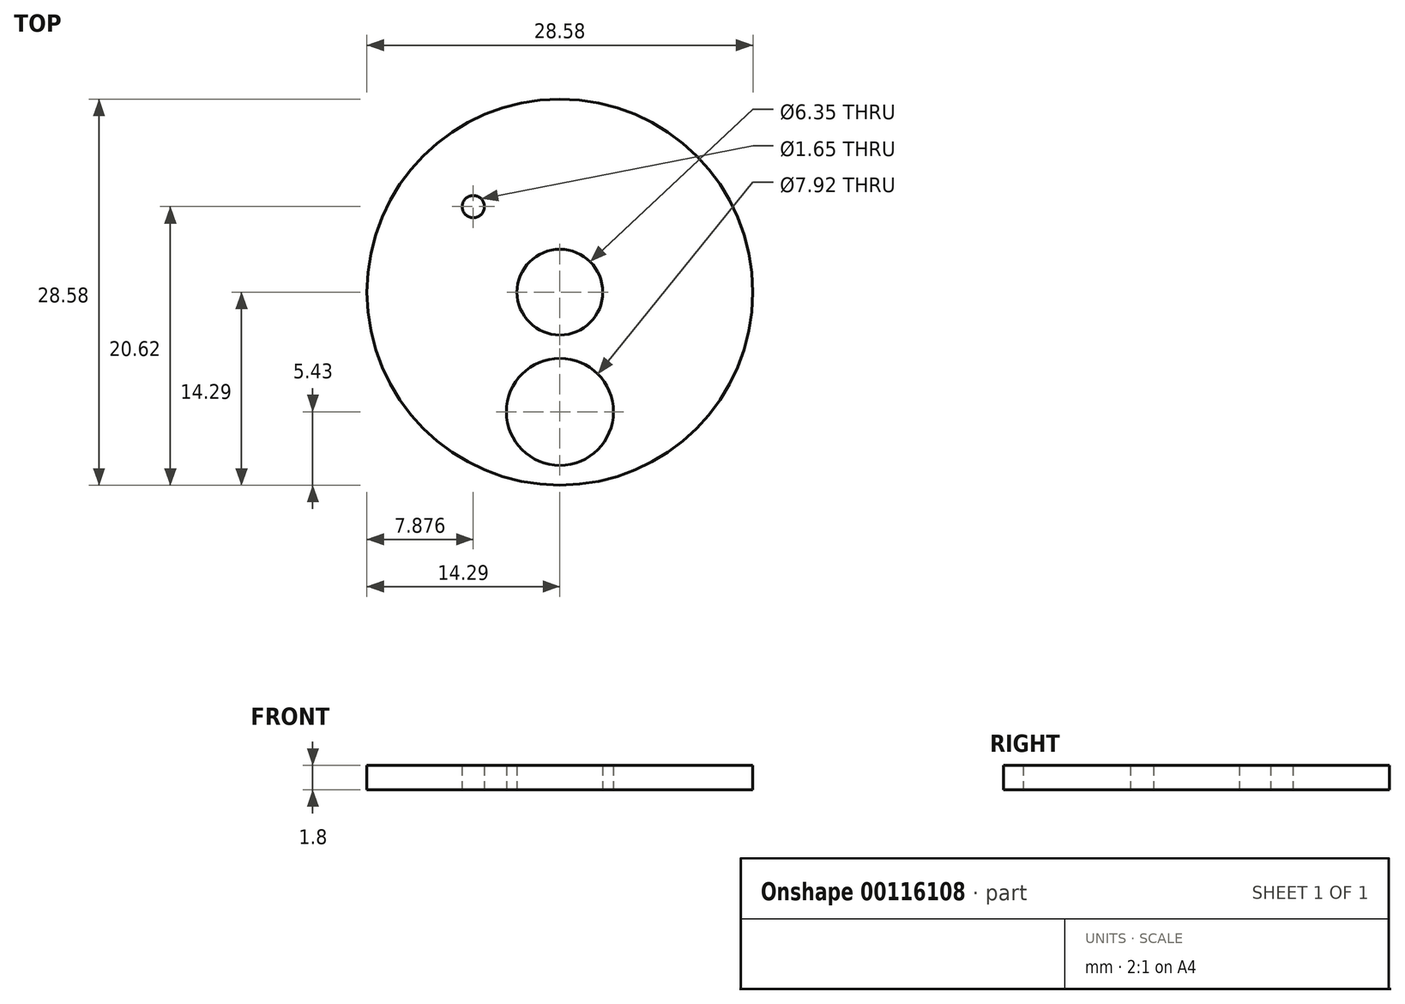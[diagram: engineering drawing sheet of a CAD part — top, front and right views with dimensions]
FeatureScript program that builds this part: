
annotation { "Feature Type Name" : "Feature", "Feature Type Description" : "" }
export const myFeature = defineFeature(function(context is Context, id is Id, definition is map)
    precondition{}
    {
        {
            var Q0;
            Q0=qCreatedBy(makeId("Top.planeOp"),FACE);
            var sketch = newSketch(context, id + "F0", { "sketchPlane" : qUnion([Q0])});
            skCircle(sketch, "E0", {"center": v(0, 0) * mm, "radius": 14.29 * mm});
            skCircle(sketch, "E1", {"center": v(0, 0) * mm, "radius": 3.18 * mm});
            skCircle(sketch, "E2", {"center": v(-6.41, 6.33) * mm, "radius": 0.83 * mm});
            skCircle(sketch, "E3", {"center": v(0, -8.86) * mm, "radius": 3.96 * mm});
            skSolve(sketch);
        }
        {
            var Q0;
            Q0=makeQuery(id+"F0.imprint","IMPRINT",FACE,{"disambiguationData":[TD([[makeQuery(id+"F0.imprint","IMPRINT",EDGE,{"derivedFrom":sQuery(id+"F0.wireOp",EDGE,"E0")}),1.0]])]});
            extrude(context, id + "F1", {"entities" : qUnion([Q0]), "depth" : 1.8 * mm});
        }
    });
